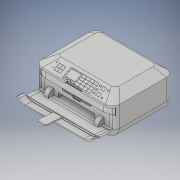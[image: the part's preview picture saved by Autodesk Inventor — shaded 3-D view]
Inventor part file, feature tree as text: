
AUTODESK INVENTOR PART (.ipt)
format: ipt  version: 2017 (Build 210142000, 142)  size: 1,312,768 bytes
history: native  units: in
note: dims shown in document units (in); Inventor stores cm internally (conversion verified against a paired STEP export)
features: sketch x24, extrude x18, other x8, fillet x5, loft x3, mirror x1, plane x1
ambient origin geometry x8: Origin, YZ Plane, XZ Plane, XY Plane, X Axis, Y Axis, Z Axis, Center Point
bodies: Solid1 (feature_tree)
feature tree (60):
  extrude  "middle of body"  Depth=1.276in
  other  "top of printer"
  loft  "top part of printer"
  extrude  "keys for printer"  Depth=0.1257in
  other  "Bottom of printer"
  loft  "bottom part of printer"
  extrude  "front bottom door slot"  Depth=0.0755in
  extrude  "front top door slot"  TaperAngle=0.0deg  [1 undecoded]
  extrude  "cords cut"  Depth=0.7135in
  extrude  "cords join curve part"  Depth=0.1007in
  extrude  "paper eject slot"  TaperAngle=0.0deg  [1 undecoded]
  other  "paper eject curve up and out"
  extrude  "2nd to top slot"  Depth=0.3692in
  extrude  "2nd to bottom slot"  Depth=0.0833in
  extrude  "top slot"  Depth=0.06in
  extrude  "slot for paper rezevor"  Depth=0.0157in
  extrude  "seams for paper rezevor"  Depth=0.0481in
  other  "door axle"
  mirror  "axle for door"
  sketch  "Sketch26"  dims[d39=0.1506in d40=0.0481in]
  other  "end of door connection"
  loft  "connection from door axle to door"
  plane  "Work Plane8"
  extrude  "tray"  Depth=0.0682in
  extrude  "curve to tray to match receive"  Depth=0.0437in
  extrude  "curve to tray to match receive top"  Depth=0.0725in
  extrude  "extention for paper slot"  Depth=0.1404in TaperAngle=0.0deg
  other  "bottom of extention for paper"
  extrude  "extention for paper"  Depth=0.1207in
  extrude  "extention for paper retract area"  Depth=0.2029in
  fillet  "curve 2nd from bottom"  [1 undecoded]
  fillet  "curve top and 2nd from top"  Radius=0.3776in
  fillet  "curve extention for door"  Radius=0.0892in
  fillet  "curve door, receive door, and axles"  Radius=0.2029in
  fillet  "smooth slots"  [1 undecoded]
  sketch  "Sketch1"  dims[d3=0.151in d4=1.276in]
  sketch  "Sketch2"  dims[d5=0.151in d6=0.8125in]
  other  "Edges1"
  sketch  "Sketch3"  dims[d7=0.4346in d8=0.0in d9=0.1257in]
  other  "Edges2"
  sketch  "Sketch4"  dims[d10=0.6016in d11=0.8594in]
  sketch  "Sketch5"  dims[d12=0.151in d13=0.0755in]
  sketch  "Sketch7"  dims[d14=0.0in d15=90.0deg d16=0.0in d17=90.0deg]
  sketch  "Sketch9"  dims[d18=0.1785in d19=0.7135in]
  sketch  "Sketch15"  dims[d21=0.0833in d22=0.1007in]
  sketch  "Sketch21"  dims[d23=0.0in d24=90.0deg d25=0.0in d26=90.0deg]
  sketch  "Sketch22"  dims[d27=0.3846in d30=0.3692in]
  sketch  "Sketch23"  dims[d31=0.1158in d32=0.0in d33=0.0833in]
  sketch  "Sketch24"  dims[d34=0.1158in d35=0.0in d36=0.06in]
  sketch  "Sketch25"  dims[d37=0.0215in d38=0.0157in]
  sketch  "Sketch28"  dims[d43=0.0618in d46=0.0175in]
  sketch  "Sketch29"  dims[d47=0.0361in d48=0.0682in]
  sketch  "Sketch30"  dims[d49=0.2541in d50=0.0in d57=0.0437in]
  sketch  "Sketch31"  dims[d62=0.0142in d63=0.0725in]
  sketch  "Sketch32"  dims[d64=0.0505in d65=0.1404in d66=0.0in]
  sketch  "Sketch33"  dims[d87=1.3229in d96=0.1207in]
  sketch  "Sketch34"  dims[d97=0.0985in d98=0.474in d99=90.0deg d116=0.3776in d117=0.0892in d118=0.2029in d119=0.0in d120=180.0deg]
  sketch  "Sketch35"  dims[d121=0.3013in]
  sketch  "Sketch37"  dims[d122=0.0706in]
  sketch  "Sketch39"  dims[d123=0.0645in d124=0.0in d125=0.0327in d126=0.0758in d127=0.0143in d128=0.0in d129=0.1667in d130=0.0308in d131=0.0in d138=0.0618in d139=0.0061in d140=0.0in d141=90.0deg d142=0.0in d143=90.0deg d144=0.0344in d146=0.0618in d147=0.0in d153=0.089in d154=0.2541in d155=0.5725in d164=0.017in d165=0.0361in d167=0.0618in d168=0.0in d174=0.0142in d175=0.0725in d176=0.051in d177=0.1404in d178=0.0in d179=0.4179in d180=0.0282in d181=0.1717in d182=0.0134in d183=0.1865in d184=0.0in d185=-0.1775in d186=0.1775in d187=0.024in d188=0.0021in d189=0.5209in d190=0.0in d191=0.1796in d192=0.1796in d193=0.0in d194=0.0133in d195=0.0251in d197=0.0251in d198=0.003in d199=0.003in d201=0.0612in d202=0.0612in d203=0.012in d204=0.3333in d206=0.094in d207=0.0in d218=0.006in d219=0.006in d220=0.006in d221=0.001in d222=0.0in d223=0.3254in d224=0.2719in d226=0.0022in d227=0.0022in d229=0.0022in d230=0.0022in d232=0.0022in d236=0.0022in d238=0.0022in d243=0.0022in d244=0.0022in d245=0.0022in d246=0.0022in d247=0.0022in d248=0.0022in d249=1.1811in d251=360.0deg d253=0.0022in d270=0.0022in d271=0.0022in d272=0.005in d273=0.0in d274=0.0318in d275=0.0073in d276=0.0022in d278=0.0011in d279=0.0022in d280=0.0022in d281=0.0022in d282=0.0022in d283=0.0022in d284=0.1306in d285=0.1306in d286=0.0022in d287=0.0022in d288=0.2002in d289=0.1512in d290=0.0022in d291=0.0022in d292=0.0022in d293=0.0022in d294=0.0022in d295=0.0022in d297=0.0194in d298=0.0035in d299=0.0022in d300=0.0135in d301=0.0503in d302=0.0808in d305=0.0774in d306=0.0352in d308=0.0968in d309=0.0109in d310=0.0022in d311=0.0043in d312=0.0043in d313=0.0022in d314=0.0022in d315=0.0022in d316=0.0022in d317=0.0667in d318=0.0667in d319=0.0135in d320=0.0785in d321=0.0203in d322=0.0203in d323=0.0022in d324=0.0296in d325=0.0619in d327=0.0299in d328=0.0295in d329=0.032in d331=0.0415in d332=0.0336in d333=0.0122in d334=0.0033in d335=0.0825in]
note: 4 required parameter values undecoded (feature->parameter linkage not recoverable at this tier; creation-order binding heuristic only, values carry confidence <= 0.55)
